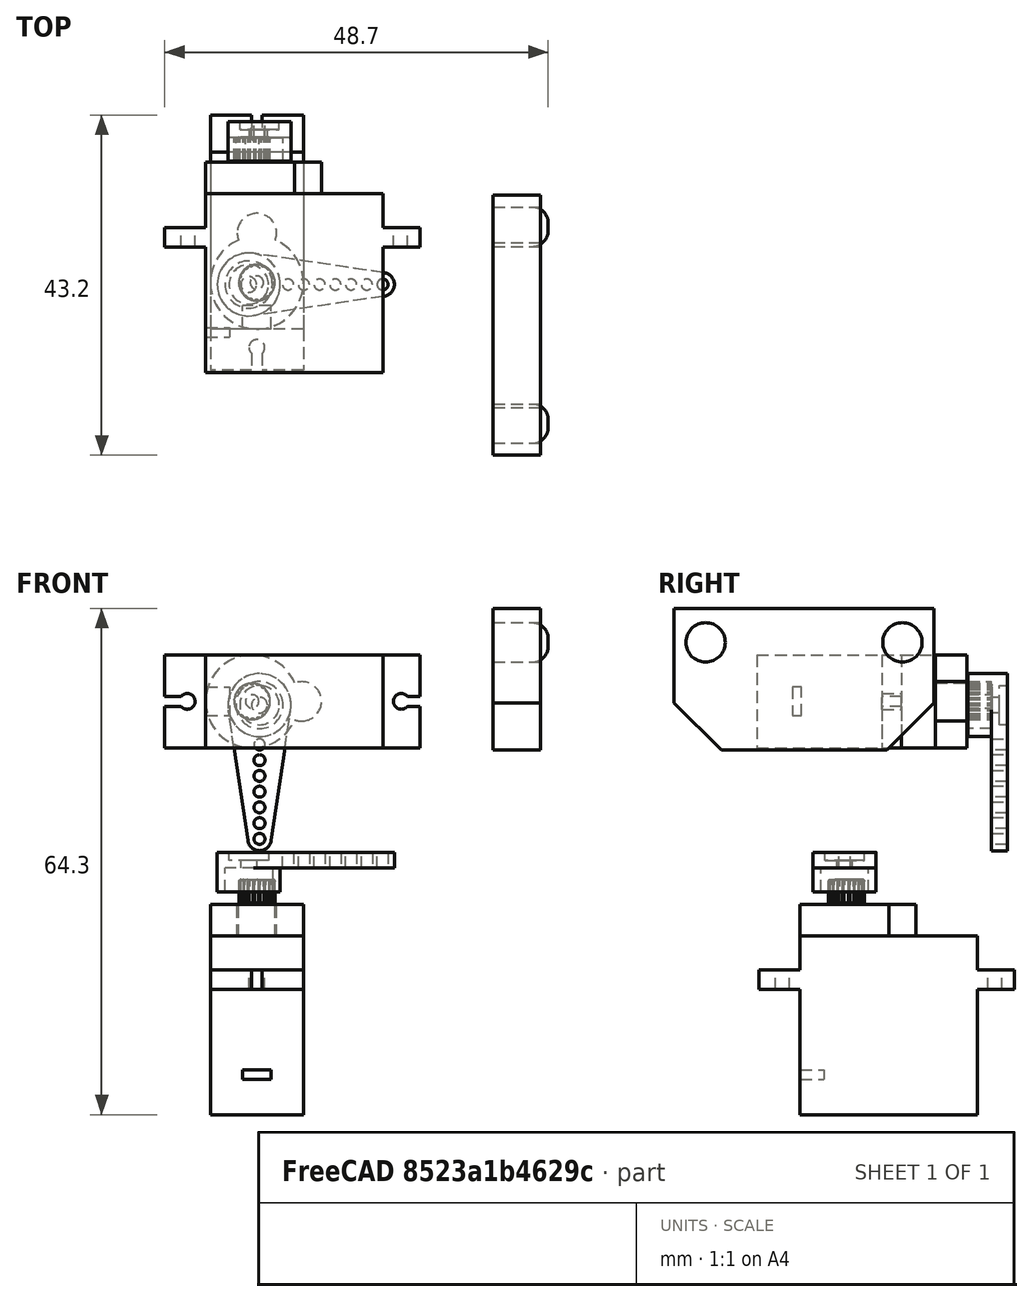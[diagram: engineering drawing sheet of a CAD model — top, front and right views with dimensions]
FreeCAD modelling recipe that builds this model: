
FCSTD DOCUMENT  (FreeCAD 0.15R4671 (Git))
Label: reto2_diseño
License: All rights reserved
LicenseURL: http://es.wikipedia.org/wiki/Todos_los_derechos_reservados
objects: Part::Feature×9, Part::Cylinder×4, Mesh::Feature×2, Part::Fillet×2, Part::Box×1, Part::Chamfer×1, Part::MultiFuse×1, Part::Cut×1
note: 19 computed .brp shape members not serialized (recipe doc carries the construction recipe); baked Part::Feature solids carry a one-line shape summary decoded from their .brp

FEATURE [Mesh::Feature] base
FEATURE [Mesh::Feature] head_with_horns
FEATURE [Part::Feature] base001
  shape: bbox 64 x 64 x 28 mm, 7446 faces, 0 solids (baked)
FEATURE [Part::Feature] head_with_horns001
  shape: bbox 40.28 x 40.28 x 34.75 mm, 6814 faces, 0 solids (baked)
FEATURE [Part::Feature] base001001  label="base002"
  Placement = pos=(0,0,0) rot=(1,0,0;3.14159rad)
  shape: bbox 64 x 64 x 28 mm, 6398 faces, 0 solids (baked)
FEATURE [Part::Feature] head_with_horns001001  label="head_with_horns002"
  shape: bbox 40.28 x 40.28 x 34.75 mm, 6357 faces, 0 solids (baked)
FEATURE [Part::Feature] arm__1_  label="arm__1_002"
  shape: bbox 47.26 x 19.94 x 11.8 mm, 913 faces, 0 solids (baked)
FEATURE [Part::Box] Box  label="Cubo"
  Height = 18
  Length = 6
  Placement = pos=(30,-22,47.3) rot=(0,0,1;0rad)
  Width = 33
FEATURE [Part::Cylinder] Cylinder  label="Cilindro"
  Angle = 360
  Height = 10
  Placement = pos=(28,7,61) rot=(0,1,0;1.5708rad)
  Radius = 2.5
FEATURE [Part::Cylinder] Cylinder001  label="Cilindro001"
  Angle = 360
  Height = 10
  Placement = pos=(28,-18,61) rot=(0,1,0;1.5708rad)
  Radius = 2.5
FEATURE [Part::Chamfer] Chamfer
  Base = -> Box
  Edges = 2 edges r=6: [Edge9,Edge11]
FEATURE [Part::MultiFuse] Fusion
  Shapes = -> [Cylinder001,Cylinder]
FEATURE [Part::Cut] Cut  label="soporte leds"
  Base = -> Chamfer
  Tool = -> Fusion
FEATURE [Part::Feature] Fusion001  label="servo inferior"
  Placement = pos=(0,16.5,1) rot=(0,0,1;3.14159rad)
  shape: bbox 11.8 x 32.4 x 29.9 mm, 77 faces (baked)
FEATURE [Part::Feature] Pocket  label="soporte servo sup"
  Placement = pos=(0.3362,20.3278,53.0303) rot=(0.57735,0.57735,-0.57735;2.0944rad)
  shape: bbox 8 x 5 x 22.5 mm, 19 faces (baked)
FEATURE [Part::Feature] Fusion002  label="servo superior"
  Placement = pos=(16,-11.5,53.5) rot=(0.57735,-0.57735,-0.57735;4.18879rad)
  shape: bbox 32.4 x 29.9 x 11.8 mm, 77 faces (baked)
FEATURE [Part::Feature] Pocket001  label="soporte servo inf"
  Placement = pos=(-1.03029,-0.3362,34.3278) rot=(1,0,0;3.14159rad)
  shape: bbox 22.5 x 8 x 5 mm, 19 faces (baked)
FEATURE [Part::Cylinder] Cylinder002  label="Cilindro002"
  Angle = 360
  Height = 7
  Placement = pos=(70,0,0) rot=(0,0,1;0rad)
  Radius = 2.5
FEATURE [Part::Fillet] Fillet  label="LED1"
  Base = -> Cylinder002
  Edges = 1 edges r=2: [Edge1]
  Placement = pos=(30,7,131) rot=(0,1,0;1.5708rad)
FEATURE [Part::Cylinder] Cylinder003  label="Cilindro003"
  Angle = 360
  Height = 7
  Placement = pos=(70,0,0) rot=(0,0,1;0rad)
  Radius = 2.5
FEATURE [Part::Fillet] Fillet001  label="LED2"
  Base = -> Cylinder003
  Edges = 1 edges r=2: [Edge1]
  Placement = pos=(30,-18,131) rot=(0,1,0;1.5708rad)
